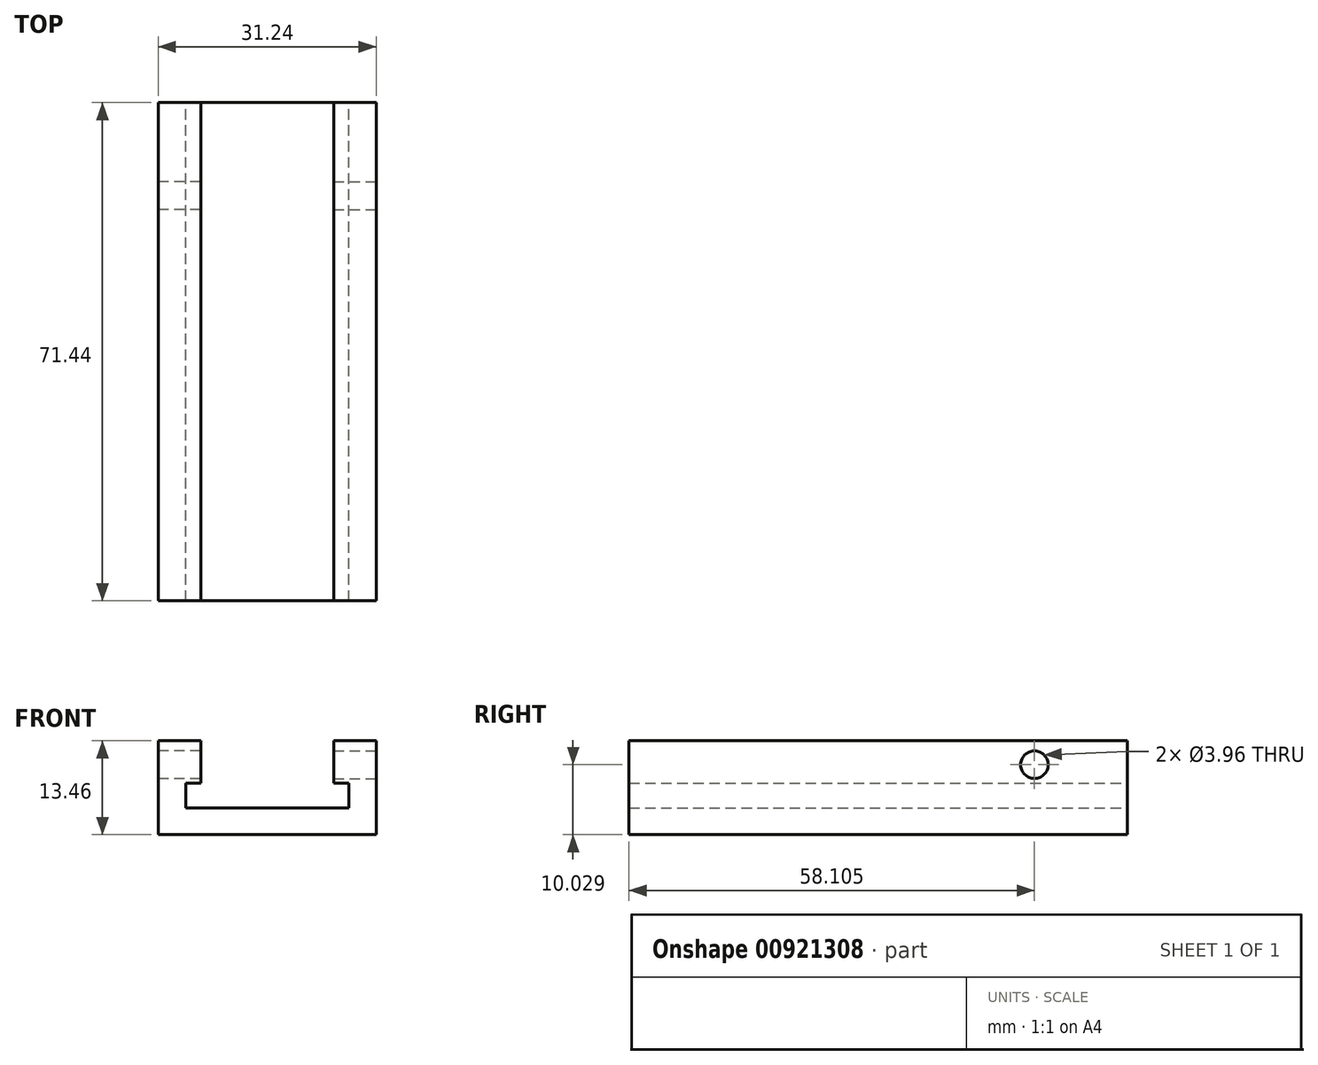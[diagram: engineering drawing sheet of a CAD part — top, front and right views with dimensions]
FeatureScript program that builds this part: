
annotation { "Feature Type Name" : "Feature", "Feature Type Description" : "" }
export const myFeature = defineFeature(function(context is Context, id is Id, definition is map)
    precondition{}
    {
        {
            var Q0;
            Q0=qCreatedBy(makeId("Front.planeOp"),FACE);
            var sketch = newSketch(context, id + "F0", { "sketchPlane" : qUnion([Q0])});
            skLineSegment(sketch, "E0", {"start": v(3.18, 12.19) * mm, "end": v(-2.91, 12.19) * mm});
            skLineSegment(sketch, "E1", {"start": v(-2.91, 12.19) * mm, "end": v(-2.91, -1.27) * mm});
            skLineSegment(sketch, "E2", {"start": v(-2.91, -1.27) * mm, "end": v(28.33, -1.27) * mm});
            skLineSegment(sketch, "E3", {"start": v(28.33, -1.27) * mm, "end": v(28.33, 12.19) * mm});
            skLineSegment(sketch, "E4", {"start": v(28.33, 12.19) * mm, "end": v(22.23, 12.19) * mm});
            skLineSegment(sketch, "E5", {"start": v(22.23, 12.19) * mm, "end": v(22.23, 6.1) * mm});
            skLineSegment(sketch, "E6", {"start": v(22.23, 6.1) * mm, "end": v(24.4, 6.1) * mm});
            skLineSegment(sketch, "E7", {"start": v(24.4, 6.1) * mm, "end": v(24.4, 2.54) * mm});
            skLineSegment(sketch, "E8", {"start": v(24.4, 2.54) * mm, "end": v(1.02, 2.54) * mm});
            skLineSegment(sketch, "E9", {"start": v(1.02, 2.54) * mm, "end": v(1.02, 6.1) * mm});
            skLineSegment(sketch, "E10", {"start": v(1.02, 6.1) * mm, "end": v(3.18, 6.1) * mm});
            skLineSegment(sketch, "E11", {"start": v(3.18, 6.1) * mm, "end": v(3.18, 12.19) * mm});
            skSolve(sketch);
        }
        {
            var Q0;
            Q0=makeQuery(id+"F0.imprint","IMPRINT",FACE,{"disambiguationData":[TD([[makeQuery(id+"F0.imprint","IMPRINT",EDGE,{"derivedFrom":sQuery(id+"F0.wireOp",EDGE,"E0")}),1.0]])]});
            extrude(context, id + "F1", {"entities" : qUnion([Q0]), "depth" : 71.44 * mm, "offsetDistance" : 25.4 * mm});
        }
        {
            var Q0;
            Q0=makeQuery(id+"F1.opExtrude","SWEPT_FACE",FACE,{"disambiguationData":[OSD([sQuery(id+"F0.wireOp",EDGE,"E3")])]});
            var sketch = newSketch(context, id + "F2", { "sketchPlane" : qUnion([Q0])});
            skCircle(sketch, "E12", {"center": v(-13.33, 8.76) * mm, "radius": 1.98 * mm});
            skSolve(sketch);
        }
        {
            var Q0;
            Q0=makeQuery(id+"F2.imprint","IMPRINT",FACE,{"disambiguationData":[TD([[makeQuery(id+"F2.imprint","IMPRINT",EDGE,{"derivedFrom":sQuery(id+"F2.wireOp",EDGE,"E12")}),1.0]])]});
            var Q1;
            Q1=sQuery(id+"F2.wireOp",EDGE,"E12");
            extrude(context, id + "F3", {"entities" : qUnion([Q0]), "operationType" : NewBodyOperationType.REMOVE, "surfaceEntities" : qUnion([Q1]), "endBound" : BoundingType.UP_TO_NEXT, "oppositeDirection" : true, "depth" : 25.4 * mm, "offsetDistance" : 25.4 * mm});
        }
        {
            var Q0;
            Q0=makeQuery(id+"F1.opExtrude","SWEPT_FACE",FACE,{"disambiguationData":[OSD([sQuery(id+"F0.wireOp",EDGE,"E1")])]});
            var sketch = newSketch(context, id + "F4", { "sketchPlane" : qUnion([Q0])});
            skCircle(sketch, "E13", {"center": v(13.34, 8.76) * mm, "radius": 1.98 * mm});
            skSolve(sketch);
        }
        {
            var Q0;
            Q0 = qSketchRegion(id + "F4", true);
            extrude(context, id + "F5", {"entities" : qUnion([Q0]), "operationType" : NewBodyOperationType.REMOVE, "endBound" : BoundingType.UP_TO_NEXT, "oppositeDirection" : true, "depth" : 25.4 * mm, "offsetDistance" : 25.4 * mm});
        }
    });
